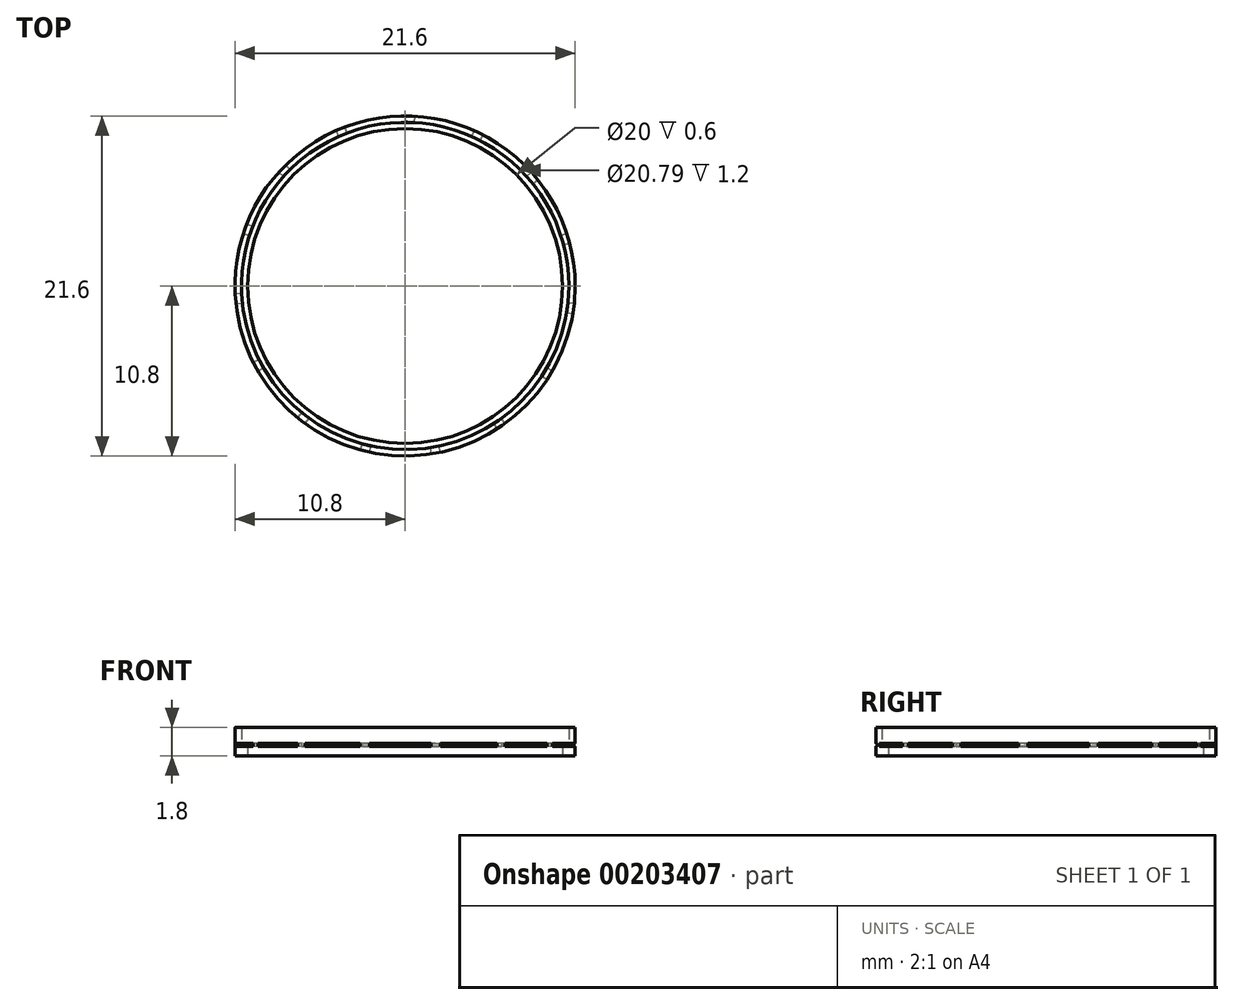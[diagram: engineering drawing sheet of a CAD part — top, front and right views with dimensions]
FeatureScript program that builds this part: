
annotation { "Feature Type Name" : "Feature", "Feature Type Description" : "" }
export const myFeature = defineFeature(function(context is Context, id is Id, definition is map)
    precondition{}
    {
        {
            var Q0;
            Q0=qCreatedBy(makeId("Top.planeOp"),FACE);
            var sketch = newSketch(context, id + "F0", { "sketchPlane" : qUnion([Q0])});
            skCircle(sketch, "E0", {"center": v(0, 0) * mm, "radius": 10.8 * mm});
            skCircle(sketch, "E1", {"center": v(0, 0) * mm, "radius": 10 * mm});
            skSolve(sketch);
        }
        {
            var Q0;
            Q0=qSketchRegion(id+"F0",true);
            extrude(context, id + "F1", {"entities" : qUnion([Q0]), "depth" : .6 * mm});
        }
        {
            var Q0;
            Q0=makeQuery(id+"F1.opExtrude","CAP_FACE",FACE,{"disambiguationData":[OSD([sQuery(id+"F0.wireOp",EDGE,"E0"),sQuery(id+"F0.wireOp",EDGE,"E1")])],"isStart":false});
            var sketch = newSketch(context, id + "F2", { "sketchPlane" : qUnion([Q0])});
            skArc(sketch, "E2", {"start": v(0.6, 10.38) * mm, "mid": v(0.3, 10.4) * mm, "end": v(0, 10.4) * mm});
            skLineSegment(sketch, "E3", {"start": v(0, 10.8) * mm, "end": v(0, 10.4) * mm});
            skLineSegment(sketch, "E4", {"start": v(0, 0) * mm, "end": v(0.62, 10.78) * mm, "construction": true});
            skLineSegment(sketch, "E5", {"start": v(0.6, 10.38) * mm, "end": v(0.62, 10.78) * mm});
            skLineSegment(sketch, "E6", {"start": v(0, 10.8) * mm, "end": v(0.62, 10.78) * mm});
            skLineSegment(sketch, "E7.1.0", {"start": v(-4.4, 9.87) * mm, "end": v(-4.23, 9.5) * mm});
            skLineSegment(sketch, "E7.1.1", {"start": v(-4.4, 9.87) * mm, "end": v(-3.82, 10.1) * mm});
            skLineSegment(sketch, "E7.1.2", {"start": v(-3.67, 9.72) * mm, "end": v(-3.82, 10.1) * mm});
            skArc(sketch, "E7.1.3", {"start": v(-3.67, 9.72) * mm, "mid": v(-3.95, 9.61) * mm, "end": v(-4.23, 9.5) * mm});
            skLineSegment(sketch, "E7.2.0", {"start": v(-8.03, 7.23) * mm, "end": v(-7.73, 6.96) * mm});
            skLineSegment(sketch, "E7.2.1", {"start": v(-8.03, 7.23) * mm, "end": v(-7.6, 7.68) * mm});
            skLineSegment(sketch, "E7.2.2", {"start": v(-7.31, 7.4) * mm, "end": v(-7.6, 7.68) * mm});
            skArc(sketch, "E7.2.3", {"start": v(-7.31, 7.4) * mm, "mid": v(-7.52, 7.18) * mm, "end": v(-7.73, 6.96) * mm});
            skLineSegment(sketch, "E7.3.0", {"start": v(-10.27, 3.34) * mm, "end": v(-9.89, 3.21) * mm});
            skLineSegment(sketch, "E7.3.1", {"start": v(-10.27, 3.34) * mm, "end": v(-10.06, 3.92) * mm});
            skLineSegment(sketch, "E7.3.2", {"start": v(-9.68, 3.78) * mm, "end": v(-10.06, 3.92) * mm});
            skArc(sketch, "E7.3.3", {"start": v(-9.68, 3.78) * mm, "mid": v(-9.79, 3.5) * mm, "end": v(-9.89, 3.21) * mm});
            skLineSegment(sketch, "E7.4.0", {"start": v(-10.74, -1.13) * mm, "end": v(-10.34, -1.09) * mm});
            skLineSegment(sketch, "E7.4.1", {"start": v(-10.74, -1.13) * mm, "end": v(-10.79, -0.5) * mm});
            skLineSegment(sketch, "E7.4.2", {"start": v(-10.38, -0.49) * mm, "end": v(-10.79, -0.5) * mm});
            skArc(sketch, "E7.4.3", {"start": v(-10.38, -0.49) * mm, "mid": v(-10.37, -0.79) * mm, "end": v(-10.34, -1.09) * mm});
            skLineSegment(sketch, "E7.5.0", {"start": v(-9.35, -5.4) * mm, "end": v(-9, -5.2) * mm});
            skLineSegment(sketch, "E7.5.1", {"start": v(-9.35, -5.4) * mm, "end": v(-9.65, -4.85) * mm});
            skLineSegment(sketch, "E7.5.2", {"start": v(-9.29, -4.67) * mm, "end": v(-9.65, -4.85) * mm});
            skArc(sketch, "E7.5.3", {"start": v(-9.29, -4.67) * mm, "mid": v(-9.15, -4.94) * mm, "end": v(-9, -5.2) * mm});
            skLineSegment(sketch, "E7.6.0", {"start": v(-6.35, -8.74) * mm, "end": v(-6.11, -8.41) * mm});
            skLineSegment(sketch, "E7.6.1", {"start": v(-6.35, -8.74) * mm, "end": v(-6.84, -8.36) * mm});
            skLineSegment(sketch, "E7.6.2", {"start": v(-6.59, -8.04) * mm, "end": v(-6.84, -8.36) * mm});
            skArc(sketch, "E7.6.3", {"start": v(-6.59, -8.04) * mm, "mid": v(-6.35, -8.23) * mm, "end": v(-6.11, -8.41) * mm});
            skLineSegment(sketch, "E7.7.0", {"start": v(-2.25, -10.56) * mm, "end": v(-2.16, -10.17) * mm});
            skLineSegment(sketch, "E7.7.1", {"start": v(-2.25, -10.56) * mm, "end": v(-2.85, -10.42) * mm});
            skLineSegment(sketch, "E7.7.2", {"start": v(-2.74, -10.03) * mm, "end": v(-2.85, -10.42) * mm});
            skArc(sketch, "E7.7.3", {"start": v(-2.74, -10.03) * mm, "mid": v(-2.45, -10.1) * mm, "end": v(-2.16, -10.17) * mm});
            skLineSegment(sketch, "E7.8.0", {"start": v(2.25, -10.56) * mm, "end": v(2.16, -10.17) * mm});
            skLineSegment(sketch, "E7.8.1", {"start": v(2.25, -10.56) * mm, "end": v(1.63, -10.68) * mm});
            skLineSegment(sketch, "E7.8.2", {"start": v(1.57, -10.28) * mm, "end": v(1.63, -10.68) * mm});
            skArc(sketch, "E7.8.3", {"start": v(1.57, -10.28) * mm, "mid": v(1.87, -10.23) * mm, "end": v(2.16, -10.17) * mm});
            skLineSegment(sketch, "E7.9.0", {"start": v(6.35, -8.74) * mm, "end": v(6.11, -8.41) * mm});
            skLineSegment(sketch, "E7.9.1", {"start": v(6.35, -8.74) * mm, "end": v(5.83, -9.09) * mm});
            skLineSegment(sketch, "E7.9.2", {"start": v(5.61, -8.75) * mm, "end": v(5.83, -9.09) * mm});
            skArc(sketch, "E7.9.3", {"start": v(5.61, -8.75) * mm, "mid": v(5.87, -8.58) * mm, "end": v(6.11, -8.41) * mm});
            skLineSegment(sketch, "E7.10.0", {"start": v(9.35, -5.4) * mm, "end": v(9, -5.2) * mm});
            skLineSegment(sketch, "E7.10.1", {"start": v(9.35, -5.4) * mm, "end": v(9.03, -5.93) * mm});
            skLineSegment(sketch, "E7.10.2", {"start": v(8.69, -5.7) * mm, "end": v(9.03, -5.93) * mm});
            skArc(sketch, "E7.10.3", {"start": v(8.69, -5.7) * mm, "mid": v(8.85, -5.46) * mm, "end": v(9, -5.2) * mm});
            skLineSegment(sketch, "E7.11.0", {"start": v(10.74, -1.13) * mm, "end": v(10.34, -1.09) * mm});
            skLineSegment(sketch, "E7.11.1", {"start": v(10.74, -1.13) * mm, "end": v(10.66, -1.75) * mm});
            skLineSegment(sketch, "E7.11.2", {"start": v(10.26, -1.68) * mm, "end": v(10.66, -1.75) * mm});
            skArc(sketch, "E7.11.3", {"start": v(10.26, -1.68) * mm, "mid": v(10.3, -1.38) * mm, "end": v(10.34, -1.09) * mm});
            skLineSegment(sketch, "E7.12.0", {"start": v(10.27, 3.34) * mm, "end": v(9.89, 3.21) * mm});
            skLineSegment(sketch, "E7.12.1", {"start": v(10.27, 3.34) * mm, "end": v(10.45, 2.74) * mm});
            skLineSegment(sketch, "E7.12.2", {"start": v(10.06, 2.64) * mm, "end": v(10.45, 2.74) * mm});
            skArc(sketch, "E7.12.3", {"start": v(10.06, 2.64) * mm, "mid": v(9.98, 2.93) * mm, "end": v(9.89, 3.21) * mm});
            skLineSegment(sketch, "E7.13.0", {"start": v(8.03, 7.23) * mm, "end": v(7.73, 6.96) * mm});
            skLineSegment(sketch, "E7.13.1", {"start": v(8.03, 7.23) * mm, "end": v(8.43, 6.75) * mm});
            skLineSegment(sketch, "E7.13.2", {"start": v(8.11, 6.5) * mm, "end": v(8.43, 6.75) * mm});
            skArc(sketch, "E7.13.3", {"start": v(8.11, 6.5) * mm, "mid": v(7.92, 6.73) * mm, "end": v(7.73, 6.96) * mm});
            skLineSegment(sketch, "E7.14.0", {"start": v(4.4, 9.87) * mm, "end": v(4.23, 9.5) * mm});
            skLineSegment(sketch, "E7.14.1", {"start": v(4.4, 9.87) * mm, "end": v(4.95, 9.6) * mm});
            skLineSegment(sketch, "E7.14.2", {"start": v(4.77, 9.24) * mm, "end": v(4.95, 9.6) * mm});
            skArc(sketch, "E7.14.3", {"start": v(4.77, 9.24) * mm, "mid": v(4.5, 9.37) * mm, "end": v(4.23, 9.5) * mm});
            skSolve(sketch);
        }
        {
            var Q0;
            Q0=qSketchRegion(id+"F2",true);
            extrude(context, id + "F3", {"entities" : qUnion([Q0]), "operationType" : NewBodyOperationType.ADD, "depth" : .2 * mm});
        }
        {
            var Q0;
            Q0=makeQuery(id+"F3.opExtrude","CAP_FACE",FACE,{"disambiguationData":[OSD([sQuery(id+"F2.wireOp",EDGE,"E2"),sQuery(id+"F2.wireOp",EDGE,"E3"),sQuery(id+"F2.wireOp",EDGE,"E5"),sQuery(id+"F2.wireOp",EDGE,"E6")])],"isStart":false});
            var sketch = newSketch(context, id + "F4", { "sketchPlane" : qUnion([Q0])});
            skCircle(sketch, "E8", {"center": v(0, 0) * mm, "radius": 10.8 * mm});
            skCircle(sketch, "E9", {"center": v(0, 0) * mm, "radius": 10.4 * mm});
            skSolve(sketch);
        }
        {
            var Q0;
            Q0=qSketchRegion(id+"F4",true);
            extrude(context, id + "F5", {"entities" : qUnion([Q0]), "operationType" : NewBodyOperationType.ADD, "depth" : 1 * mm});
        }
    });
